# Revit family: Towel Rail-Single-Dorf Epic1
name_source: partatom
category: Specialty Equipment
revit_build: Autodesk Revit Architecture 2012 (Build: 20110916_2132(x64)
units: mm (PartAtom-declared; Revit-internal decimal feet)

## types (2) — shared parameters
Assembly Code = C1030200
Description = In line with the current bathroom trend toward more minimally styled geometric shapes
Manufacturer = Dorf
Material_ANZRS = Metal-Chrome-Caroma
URL = http://www.dorf.com.au
zero-valued in all types: Cost

## per-type parameters (varying)
| type | Default Elevation | Length_ANZRS | Long | Model |
| Epic Single Towel Rail - 600mm | 1100 mm | 600 mm | No | 6424.04 |
| Epic Single Towel Rail - 800mm | 900 mm  [stored 2.95276 ft] | 800 mm  [stored 2.62467 ft] | Yes | 6425.04 |

note: column(s) folded — value = type name in every type: Type Comments

note: [stored X ft] marks values corroborated as IEEE doubles in the binary element streams (Revit-internal decimal feet)

## geometry (parser evidence)
native form markers: Blend x4, Sweep x1
no freeform markers — native parametric forms only
